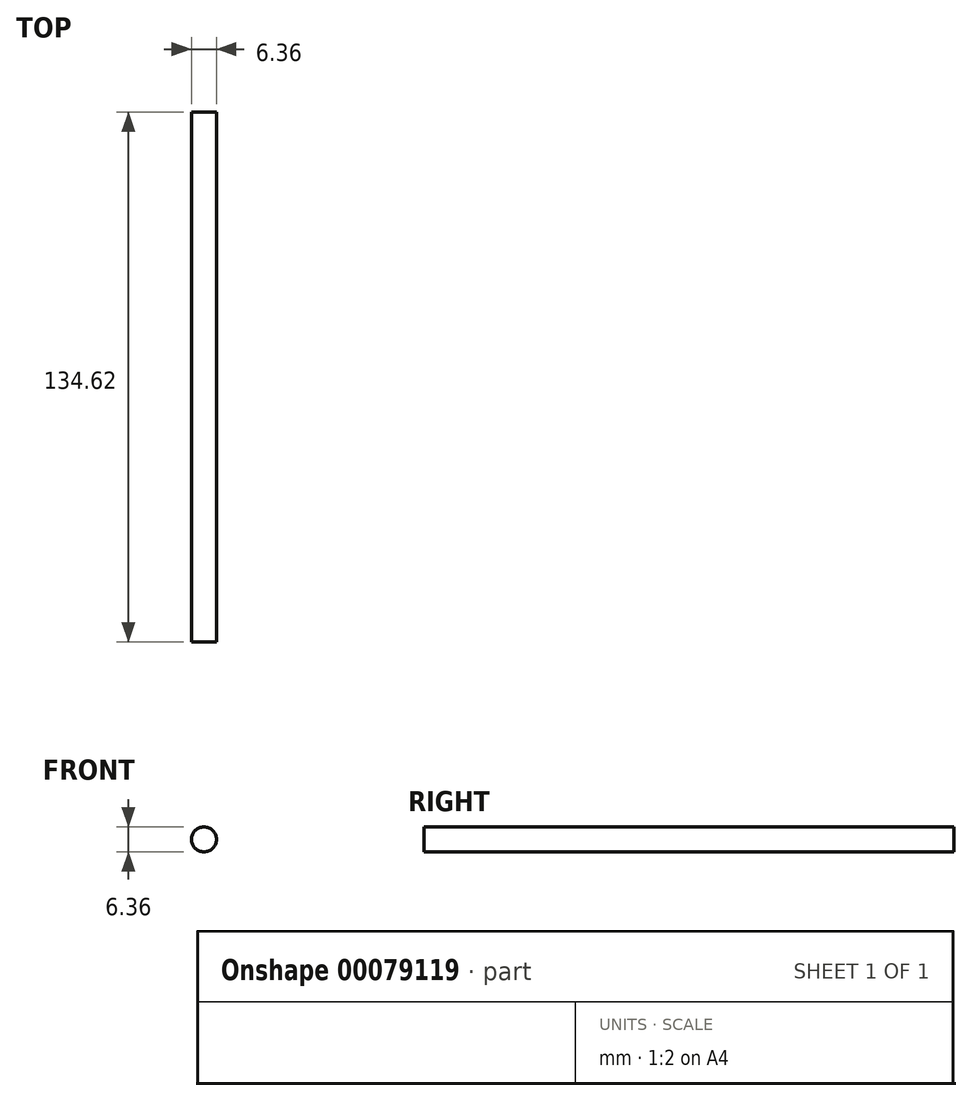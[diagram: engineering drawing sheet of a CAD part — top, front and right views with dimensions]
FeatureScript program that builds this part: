
annotation { "Feature Type Name" : "Feature", "Feature Type Description" : "" }
export const myFeature = defineFeature(function(context is Context, id is Id, definition is map)
    precondition{}
    {
        {
            var Q0;
            Q0=qCreatedBy(makeId("Front.planeOp"),FACE);
            var sketch = newSketch(context, id + "F0", { "sketchPlane" : qUnion([Q0])});
            skCircle(sketch, "E0", {"center": v(0, 0) * mm, "radius": 3.18 * mm});
            skSolve(sketch);
        }
        {
            var Q0;
            Q0 = qSketchRegion(id + "F0", true);
            extrude(context, id + "F1", {"entities" : qUnion([Q0]), "depth" : 134.62 * mm});
        }
    });
